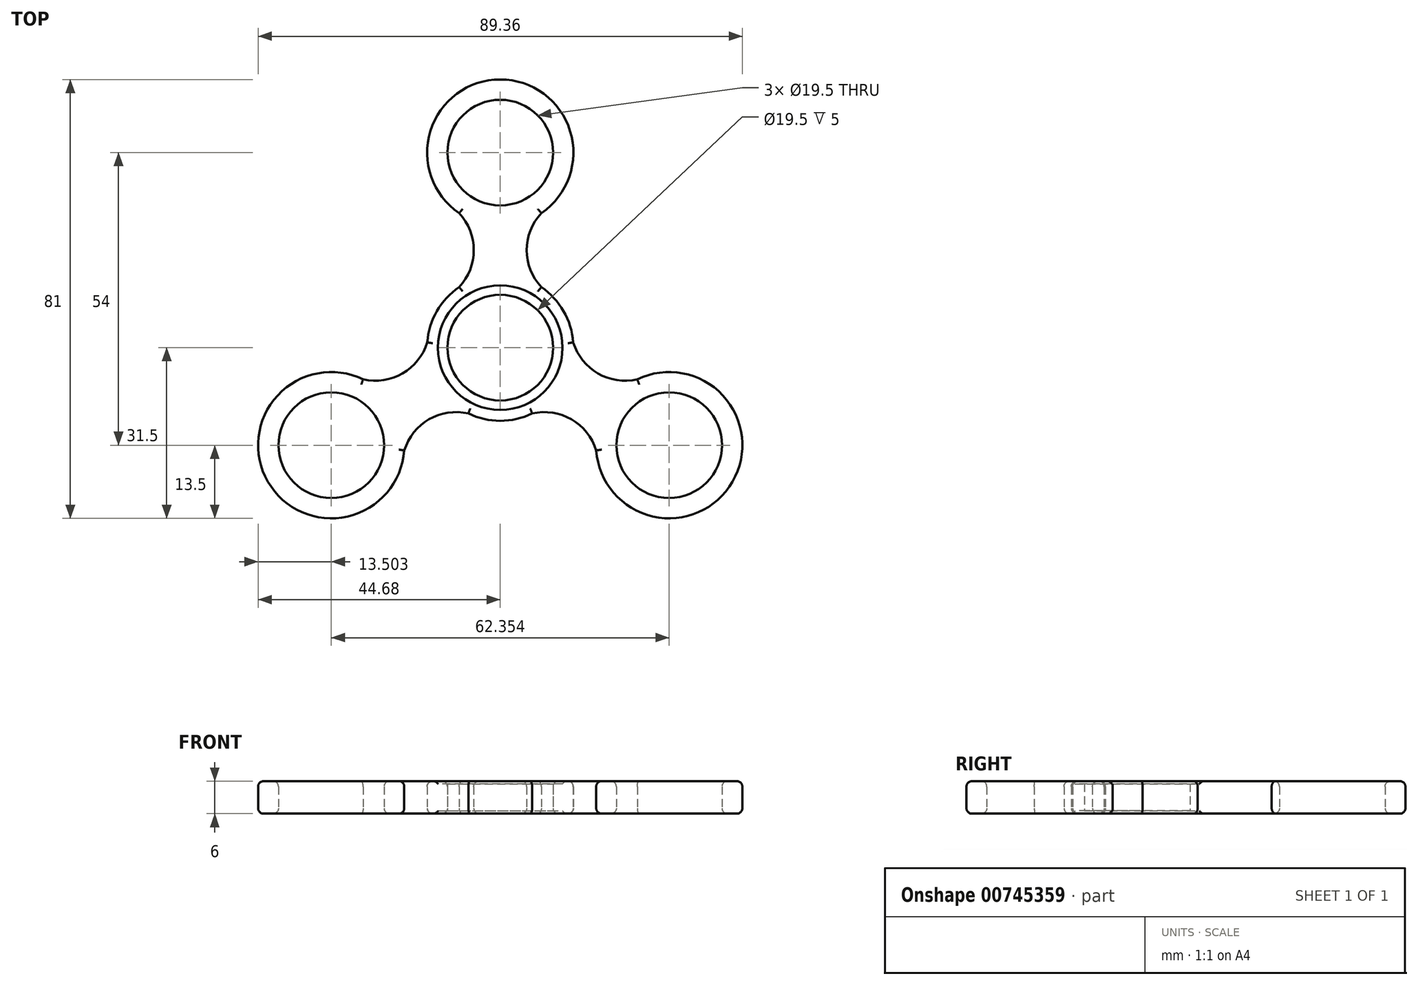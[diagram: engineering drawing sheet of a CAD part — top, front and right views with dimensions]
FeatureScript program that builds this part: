
annotation { "Feature Type Name" : "Feature", "Feature Type Description" : "" }
export const myFeature = defineFeature(function(context is Context, id is Id, definition is map)
    precondition{}
    {
        {
            var Q0;
            Q0=qCreatedBy(makeId("Top.planeOp"),FACE);
            var sketch = newSketch(context, id + "F0", { "sketchPlane" : qUnion([Q0])});
            skCircle(sketch, "E0", {"center": v(0, 0) * mm, "radius": 9.5 * mm, "construction": true});
            skLineSegment(sketch, "E1", {"start": v(0, 0) * mm, "end": v(0, 36) * mm, "construction": true});
            skCircle(sketch, "E2", {"center": v(0, 36) * mm, "radius": 9.5 * mm, "construction": true});
            skLineSegment(sketch, "E3", {"start": v(0, 0) * mm, "end": v(-31.18, -18) * mm, "construction": true});
            skLineSegment(sketch, "E4", {"start": v(0, 0) * mm, "end": v(31.18, -18) * mm, "construction": true});
            skCircle(sketch, "E5", {"center": v(31.18, -18) * mm, "radius": 9.5 * mm, "construction": true});
            skCircle(sketch, "E6", {"center": v(-31.18, -18) * mm, "radius": 9.5 * mm, "construction": true});
            skCircle(sketch, "E7", {"center": v(0, 0) * mm, "radius": 9.75 * mm});
            skCircle(sketch, "E8", {"center": v(-31.18, -18) * mm, "radius": 9.75 * mm});
            skCircle(sketch, "E9", {"center": v(31.18, -18) * mm, "radius": 9.75 * mm});
            skCircle(sketch, "E10", {"center": v(0, 36) * mm, "radius": 9.75 * mm});
            skCircle(sketch, "E11", {"center": v(31.18, -18) * mm, "radius": 13.5 * mm});
            skCircle(sketch, "E12", {"center": v(0, 36) * mm, "radius": 13.5 * mm});
            skCircle(sketch, "E13", {"center": v(-31.18, -18) * mm, "radius": 13.5 * mm});
            skCircle(sketch, "E14", {"center": v(0, 0) * mm, "radius": 13.5 * mm});
            skLineSegment(sketch, "E15", {"start": v(-31.18, -18) * mm, "end": v(-27.68, -4.96) * mm, "construction": true});
            skLineSegment(sketch, "E16", {"start": v(0, 0) * mm, "end": v(-13.04, 3.5) * mm, "construction": true});
            skArc(sketch, "E17", {"start": v(-27.68, -4.96) * mm, "mid": v(-18.03, -4.77) * mm, "end": v(-13.04, 3.5) * mm});
            skArc(sketch, "E18.MirrorCS", {"start": v(-18.14, -21.5) * mm, "mid": v(-13.14, -13.23) * mm, "end": v(-3.5, -13.04) * mm});
            skArc(sketch, "E19.MirrorCS", {"start": v(27.68, -4.96) * mm, "mid": v(18.03, -4.77) * mm, "end": v(13.04, 3.5) * mm});
            skArc(sketch, "E20.MirrorCS", {"start": v(18.14, -21.5) * mm, "mid": v(13.14, -13.23) * mm, "end": v(3.5, -13.04) * mm});
            skArc(sketch, "E21.MirrorCS", {"start": v(-9.55, 26.45) * mm, "mid": v(-4.89, 18) * mm, "end": v(-9.55, 9.55) * mm});
            skArc(sketch, "E22.MirrorCS", {"start": v(9.55, 26.45) * mm, "mid": v(4.89, 18) * mm, "end": v(9.55, 9.55) * mm});
            skSolve(sketch);
        }
        {
            var Q0;
            Q0=qSketchRegion(id+"F0",true);
            extrude(context, id + "F1", {"entities" : qUnion([Q0]), "depth" : 6 * mm, "offsetDistance" : 25 * mm});
        }
        {
            var Q0;
            Q0=makeQuery(id+"F1.opExtrude","CAP_FACE",FACE,{"disambiguationData":[OSD([sQuery(id+"F0.wireOp",EDGE,"E7"),sQuery(id+"F0.wireOp",EDGE,"E8"),sQuery(id+"F0.wireOp",EDGE,"E9"),sQuery(id+"F0.wireOp",EDGE,"E10"),sQuery(id+"F0.wireOp",EDGE,"E11"),sQuery(id+"F0.wireOp",EDGE,"E12"),sQuery(id+"F0.wireOp",EDGE,"E13"),sQuery(id+"F0.wireOp",EDGE,"E14"),sQuery(id+"F0.wireOp",EDGE,"E17"),sQuery(id+"F0.wireOp",EDGE,"E18.MirrorCS"),sQuery(id+"F0.wireOp",EDGE,"E19.MirrorCS"),sQuery(id+"F0.wireOp",EDGE,"E20.MirrorCS"),sQuery(id+"F0.wireOp",EDGE,"E21.MirrorCS"),sQuery(id+"F0.wireOp",EDGE,"E22.MirrorCS")])],"isStart":false});
            var sketch = newSketch(context, id + "F2", { "sketchPlane" : qUnion([Q0])});
            skCircle(sketch, "E23", {"center": v(0, 0) * mm, "radius": 11.5 * mm});
            skSolve(sketch);
        }
        {
            var Q0;
            Q0=qSketchRegion(id+"F2",true);
            extrude(context, id + "F3", {"entities" : qUnion([Q0]), "operationType" : NewBodyOperationType.REMOVE, "oppositeDirection" : true, "depth" : 0.5 * mm, "offsetDistance" : 25 * mm});
        }
        {
            var Q0;
            Q0=makeQuery(id+"F1.opExtrude","CAP_FACE",FACE,{"disambiguationData":[OSD([sQuery(id+"F0.wireOp",EDGE,"E7"),sQuery(id+"F0.wireOp",EDGE,"E8"),sQuery(id+"F0.wireOp",EDGE,"E9"),sQuery(id+"F0.wireOp",EDGE,"E10"),sQuery(id+"F0.wireOp",EDGE,"E11"),sQuery(id+"F0.wireOp",EDGE,"E12"),sQuery(id+"F0.wireOp",EDGE,"E13"),sQuery(id+"F0.wireOp",EDGE,"E14"),sQuery(id+"F0.wireOp",EDGE,"E17"),sQuery(id+"F0.wireOp",EDGE,"E18.MirrorCS"),sQuery(id+"F0.wireOp",EDGE,"E19.MirrorCS"),sQuery(id+"F0.wireOp",EDGE,"E20.MirrorCS"),sQuery(id+"F0.wireOp",EDGE,"E21.MirrorCS"),sQuery(id+"F0.wireOp",EDGE,"E22.MirrorCS")])],"isStart":true});
            var sketch = newSketch(context, id + "F4", { "sketchPlane" : qUnion([Q0])});
            skCircle(sketch, "E24", {"center": v(0, 0) * mm, "radius": 11.5 * mm});
            skSolve(sketch);
        }
        {
            var Q0;
            Q0=qSketchRegion(id+"F4",true);
            extrude(context, id + "F5", {"entities" : qUnion([Q0]), "operationType" : NewBodyOperationType.REMOVE, "oppositeDirection" : true, "depth" : 0.5 * mm, "offsetDistance" : 25 * mm});
        }
        {
            var Q0;
            Q0=makeQuery(id+"F1.opExtrude","CAP_FACE",FACE,{"disambiguationData":[OSD([sQuery(id+"F0.wireOp",EDGE,"E7"),sQuery(id+"F0.wireOp",EDGE,"E8"),sQuery(id+"F0.wireOp",EDGE,"E9"),sQuery(id+"F0.wireOp",EDGE,"E10"),sQuery(id+"F0.wireOp",EDGE,"E11"),sQuery(id+"F0.wireOp",EDGE,"E12"),sQuery(id+"F0.wireOp",EDGE,"E13"),sQuery(id+"F0.wireOp",EDGE,"E14"),sQuery(id+"F0.wireOp",EDGE,"E17"),sQuery(id+"F0.wireOp",EDGE,"E18.MirrorCS"),sQuery(id+"F0.wireOp",EDGE,"E19.MirrorCS"),sQuery(id+"F0.wireOp",EDGE,"E20.MirrorCS"),sQuery(id+"F0.wireOp",EDGE,"E21.MirrorCS"),sQuery(id+"F0.wireOp",EDGE,"E22.MirrorCS")])],"isStart":false});
            var Q1;
            Q1=makeQuery(id+"F1.opExtrude","CAP_FACE",FACE,{"disambiguationData":[OSD([sQuery(id+"F0.wireOp",EDGE,"E7"),sQuery(id+"F0.wireOp",EDGE,"E8"),sQuery(id+"F0.wireOp",EDGE,"E9"),sQuery(id+"F0.wireOp",EDGE,"E10"),sQuery(id+"F0.wireOp",EDGE,"E11"),sQuery(id+"F0.wireOp",EDGE,"E12"),sQuery(id+"F0.wireOp",EDGE,"E13"),sQuery(id+"F0.wireOp",EDGE,"E14"),sQuery(id+"F0.wireOp",EDGE,"E17"),sQuery(id+"F0.wireOp",EDGE,"E18.MirrorCS"),sQuery(id+"F0.wireOp",EDGE,"E19.MirrorCS"),sQuery(id+"F0.wireOp",EDGE,"E20.MirrorCS"),sQuery(id+"F0.wireOp",EDGE,"E21.MirrorCS"),sQuery(id+"F0.wireOp",EDGE,"E22.MirrorCS")])],"isStart":true});
            fillet(context, id + "F6", {"entities" : qUnion([Q0, Q1]), "radius" : 1 * mm, "tangentPropagation" : true, "allowEdgeOverflow" : false});
        }
    });
